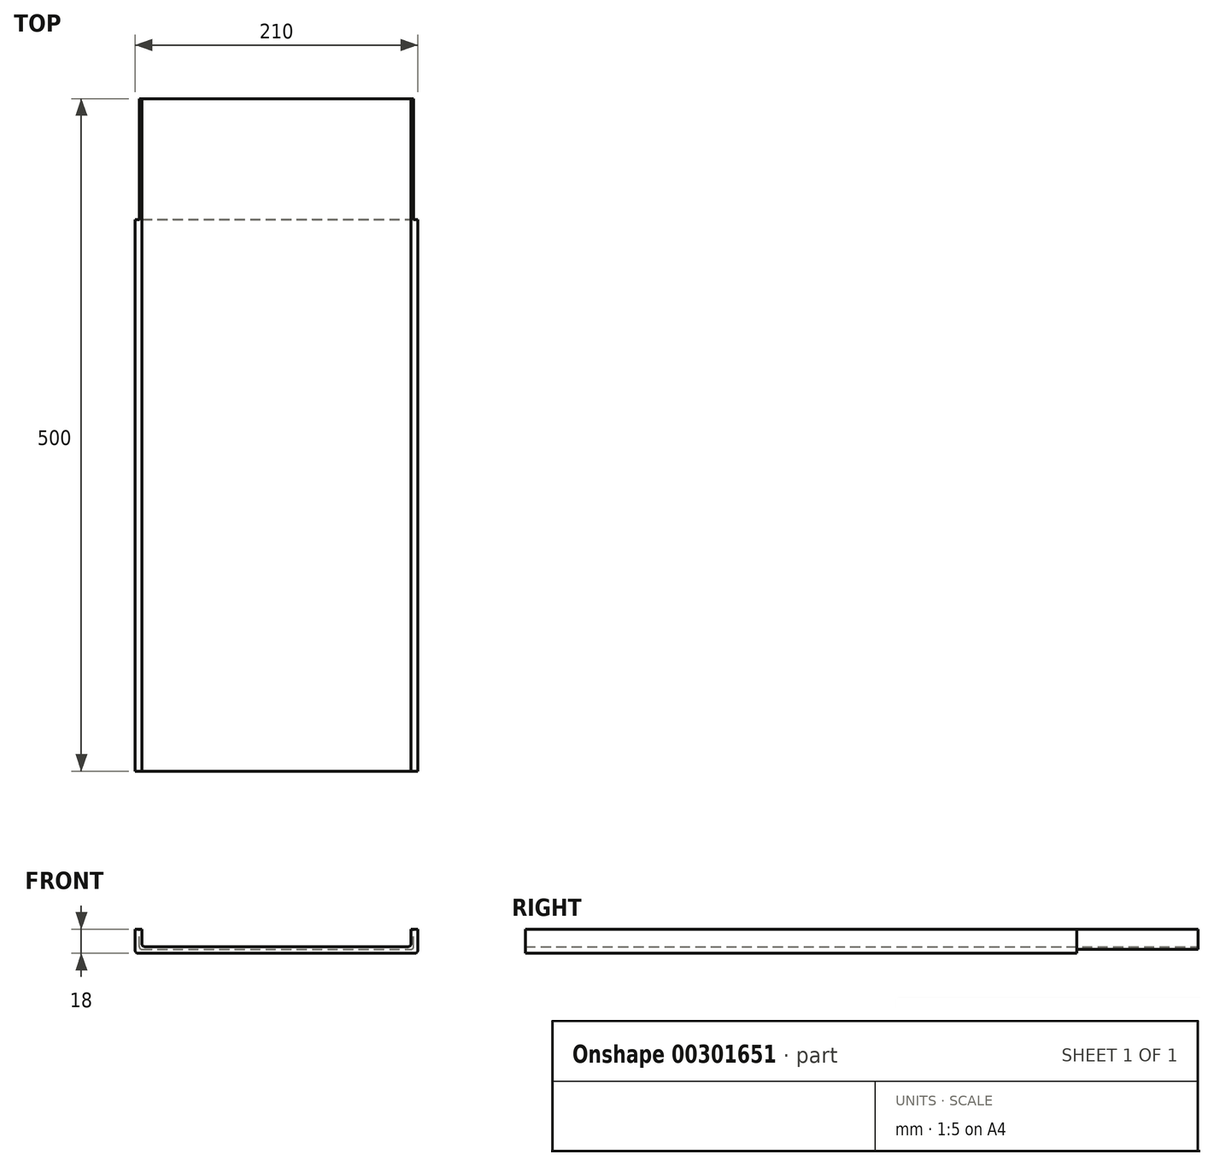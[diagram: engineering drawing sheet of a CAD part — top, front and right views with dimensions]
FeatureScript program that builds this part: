
annotation { "Feature Type Name" : "Feature", "Feature Type Description" : "" }
export const myFeature = defineFeature(function(context is Context, id is Id, definition is map)
    precondition{}
    {
        {
            var Q0;
            Q0=qCreatedBy(makeId("Front.planeOp"),FACE);
            var sketch = newSketch(context, id + "F0", { "sketchPlane" : qUnion([Q0])});
            skLineSegment(sketch, "E0.bottom", {"start": v(100, 0) * mm, "end": v(105, 0) * mm});
            skLineSegment(sketch, "E0.top", {"start": v(0, -18) * mm, "end": v(103, -18) * mm});
            skLineSegment(sketch, "E0.right", {"start": v(105, 0) * mm, "end": v(105, -16) * mm});
            skLineSegment(sketch, "E1.top", {"start": v(0, -13) * mm, "end": v(98, -13) * mm});
            skLineSegment(sketch, "E1.right", {"start": v(100, 0) * mm, "end": v(100, -11) * mm});
            skPoint(sketch, "E2.visualSharp", {"position": v(105, -18) * mm});
            skArc(sketch, "E2.filletArc", {"start": v(103, -18) * mm, "mid": v(104.41, -17.41) * mm, "end": v(105, -16) * mm});
            skPoint(sketch, "E3.visualSharp", {"position": v(100, -13) * mm});
            skArc(sketch, "E3.filletArc", {"start": v(98, -13) * mm, "mid": v(99.41, -12.41) * mm, "end": v(100, -11) * mm});
            skArc(sketch, "E4.MirrorCS", {"start": v(-98, -13) * mm, "mid": v(-99.41, -12.41) * mm, "end": v(-100, -11) * mm});
            skArc(sketch, "E5.MirrorCS", {"start": v(-103, -18) * mm, "mid": v(-104.41, -17.41) * mm, "end": v(-105, -16) * mm});
            skLineSegment(sketch, "E6.MirrorCS", {"start": v(-100, 0) * mm, "end": v(-105, 0) * mm});
            skLineSegment(sketch, "E7.MirrorCS", {"start": v(0, -13) * mm, "end": v(-98, -13) * mm});
            skLineSegment(sketch, "E8.MirrorCS", {"start": v(-100, 0) * mm, "end": v(-100, -11) * mm});
            skLineSegment(sketch, "E9.MirrorCS", {"start": v(-105, 0) * mm, "end": v(-105, -16) * mm});
            skLineSegment(sketch, "E10.MirrorCS", {"start": v(0, -18) * mm, "end": v(-103, -18) * mm});
            skPoint(sketch, "E11.MirrorP", {"position": v(-105, -18) * mm});
            skPoint(sketch, "E12.MirrorP", {"position": v(-100, -13) * mm});
            skLineSegment(sketch, "E13.bottom", {"start": v(-100, -15) * mm, "end": v(100, -15) * mm});
            skLineSegment(sketch, "E13.left", {"start": v(-102, -13) * mm, "end": v(-102, 0) * mm});
            skLineSegment(sketch, "E13.right", {"start": v(102, -13) * mm, "end": v(102, 0) * mm});
            skPoint(sketch, "E13.middle", {"position": v(0, 0) * mm});
            skPoint(sketch, "E14.orphan", {"position": v(-102, 15) * mm});
            skPoint(sketch, "E15.orphan", {"position": v(102, 15) * mm});
            skPoint(sketch, "E16.visualSharp", {"position": v(-102, -15) * mm});
            skArc(sketch, "E16.filletArc", {"start": v(-102, -13) * mm, "mid": v(-101.41, -14.41) * mm, "end": v(-100, -15) * mm});
            skPoint(sketch, "E17.visualSharp", {"position": v(102, -15) * mm});
            skArc(sketch, "E17.filletArc", {"start": v(100, -15) * mm, "mid": v(101.41, -14.41) * mm, "end": v(102, -13) * mm});
            skSolve(sketch);
        }
        {
            var Q0;
            Q0=qSketchRegion(id+"F0",true);
            extrude(context, id + "F1", {"entities" : qUnion([Q0]), "depth" : 500 * mm});
        }
        {
            var Q0;
            Q0=makeQuery(id+"F0.imprint","IMPRINT",FACE,{"disambiguationData":[TD([[makeQuery(id+"F0.imprint","IMPRINT",EDGE,{"derivedFrom":sQuery(id+"F0.wireOp",EDGE,"E0.top")}),1.0]])]});
            extrude(context, id + "F2", {"entities" : qUnion([Q0]), "operationType" : NewBodyOperationType.REMOVE, "depth" : 90 * mm});
        }
        {
            var Q0;
            Q0=qCreatedBy(makeId("Front.planeOp"),FACE);
            cPlane(context, id + "F3", {"entities" : qUnion([Q0]), "cplaneType" : CPlaneType.OFFSET, "offset" : 250 * mm, "width" : 150 * mm, "height" : 150 * mm});
        }
    });
